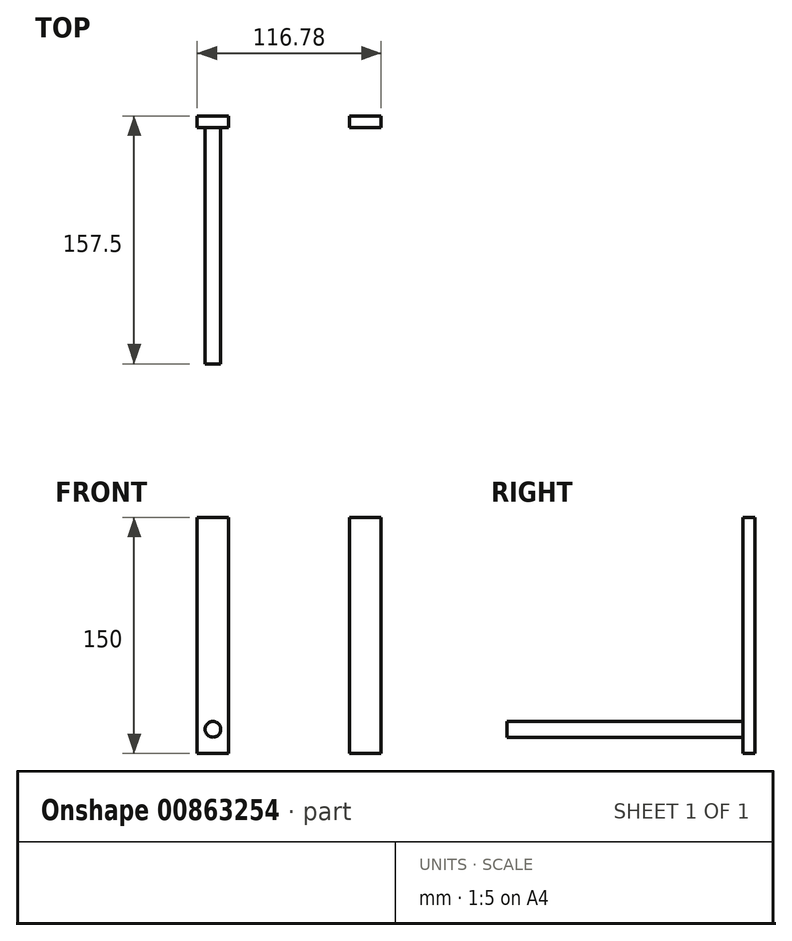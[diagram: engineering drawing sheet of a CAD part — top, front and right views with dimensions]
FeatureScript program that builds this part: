
annotation { "Feature Type Name" : "Feature", "Feature Type Description" : "" }
export const myFeature = defineFeature(function(context is Context, id is Id, definition is map)
    precondition{}
    {
        {
            var Q0;
            Q0=qCreatedBy(makeId("Front.planeOp"),FACE);
            var sketch = newSketch(context, id + "F0", { "sketchPlane" : qUnion([Q0])});
            skLineSegment(sketch, "E0.bottom", {"start": v(-38.4, -1.36) * mm, "end": v(-58.4, -1.36) * mm});
            skLineSegment(sketch, "E0.top", {"start": v(-38.4, -151.36) * mm, "end": v(-58.4, -151.36) * mm});
            skLineSegment(sketch, "E0.left", {"start": v(-38.4, -1.36) * mm, "end": v(-38.4, -151.36) * mm});
            skLineSegment(sketch, "E0.right", {"start": v(-58.4, -1.36) * mm, "end": v(-58.4, -151.36) * mm});
            skPoint(sketch, "E0.middle", {"position": v(-48.4, -76.36) * mm});
            skLineSegment(sketch, "E1.MirrorCS", {"start": v(38.4, -1.36) * mm, "end": v(38.4, -151.36) * mm});
            skLineSegment(sketch, "E2.MirrorCS", {"start": v(58.4, -1.36) * mm, "end": v(58.4, -151.36) * mm});
            skLineSegment(sketch, "E3.MirrorCS", {"start": v(38.4, -151.36) * mm, "end": v(58.4, -151.36) * mm});
            skLineSegment(sketch, "E4.MirrorCS", {"start": v(38.4, -1.36) * mm, "end": v(58.4, -1.36) * mm});
            skSolve(sketch);
        }
        {
            var Q0;
            Q0=makeQuery(id+"F0.imprint","IMPRINT",FACE,{"disambiguationData":[TD([[makeQuery(id+"F0.imprint","IMPRINT",EDGE,{"derivedFrom":sQuery(id+"F0.wireOp",EDGE,"E1.MirrorCS")}),1.0]])]});
            var Q1;
            Q1=makeQuery(id+"F0.imprint","IMPRINT",FACE,{"disambiguationData":[TD([[makeQuery(id+"F0.imprint","IMPRINT",EDGE,{"derivedFrom":sQuery(id+"F0.wireOp",EDGE,"E0.bottom")}),1.0]])]});
            extrude(context, id + "F1", {"entities" : qUnion([Q0, Q1]), "depth" : 7.5 * mm, "offsetDistance" : 25 * mm});
        }
        {
            var Q0;
            Q0=makeQuery(id+"F1.opExtrude","CAP_FACE",FACE,{"disambiguationData":[OSD([sQuery(id+"F0.wireOp",EDGE,"E1.MirrorCS"),sQuery(id+"F0.wireOp",EDGE,"E2.MirrorCS"),sQuery(id+"F0.wireOp",EDGE,"E3.MirrorCS"),sQuery(id+"F0.wireOp",EDGE,"E4.MirrorCS")])],"isStart":false});
            var Q1;
            Q1=makeQuery(id+"F1.opExtrude","CAP_FACE",FACE,{"disambiguationData":[OSD([sQuery(id+"F0.wireOp",EDGE,"E0.bottom"),sQuery(id+"F0.wireOp",EDGE,"E0.left"),sQuery(id+"F0.wireOp",EDGE,"E0.right"),sQuery(id+"F0.wireOp",EDGE,"E0.top")])],"isStart":false});
            extrude(context, id + "F2", {"entities" : qUnion([Q0, Q1]), "oppositeDirection" : true, "depth" : 7.5 * mm, "offsetDistance" : 25 * mm});
        }
        {
            var Q0;
            Q0=makeQuery(id+"F2.opExtrude","SWEPT_BODY",BODY,{"disambiguationData":[OSD([sQuery(id+"F0.wireOp",EDGE,"E0.bottom"),sQuery(id+"F0.wireOp",EDGE,"E0.left"),sQuery(id+"F0.wireOp",EDGE,"E0.right"),sQuery(id+"F0.wireOp",EDGE,"E0.top")])]});
            deleteBodies(context, id + "F3", {"entities" : qUnion([Q0])});
        }
        {
            var Q0;
            Q0=makeQuery(id+"F2.opExtrude","SWEPT_BODY",BODY,{"disambiguationData":[OSD([sQuery(id+"F0.wireOp",EDGE,"E1.MirrorCS"),sQuery(id+"F0.wireOp",EDGE,"E2.MirrorCS"),sQuery(id+"F0.wireOp",EDGE,"E3.MirrorCS"),sQuery(id+"F0.wireOp",EDGE,"E4.MirrorCS")])]});
            deleteBodies(context, id + "F4", {"entities" : qUnion([Q0])});
        }
        {
            var Q0;
            Q0=makeQuery(id+"F1.opExtrude","CAP_FACE",FACE,{"disambiguationData":[OSD([sQuery(id+"F0.wireOp",EDGE,"E0.bottom"),sQuery(id+"F0.wireOp",EDGE,"E0.left"),sQuery(id+"F0.wireOp",EDGE,"E0.right"),sQuery(id+"F0.wireOp",EDGE,"E0.top")])],"isStart":false});
            var sketch = newSketch(context, id + "F5", { "sketchPlane" : qUnion([Q0])});
            skCircle(sketch, "E5", {"center": v(-48.42, -135.96) * mm, "radius": 5 * mm});
            skCircle(sketch, "E6.MirrorC", {"center": v(48.42, -135.96) * mm, "radius": 5 * mm});
            skSolve(sketch);
        }
        {
            var Q0;
            Q0=makeQuery(id+"F5.imprint","IMPRINT",FACE,{"disambiguationData":[TD([[makeQuery(id+"F5.imprint","IMPRINT",EDGE,{"derivedFrom":sQuery(id+"F5.wireOp",EDGE,"E6.MirrorC")}),-1.0]])]});
            var Q1;
            Q1=makeQuery(id+"F5.imprint","IMPRINT",FACE,{"disambiguationData":[TD([[makeQuery(id+"F5.imprint","IMPRINT",EDGE,{"derivedFrom":sQuery(id+"F5.wireOp",EDGE,"E5")}),1.0]])]});
            extrude(context, id + "F6", {"entities" : qUnion([Q0, Q1]), "depth" : 150 * mm, "offsetDistance" : 25 * mm});
        }
    });
